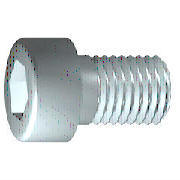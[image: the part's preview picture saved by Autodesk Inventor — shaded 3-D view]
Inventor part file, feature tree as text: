
AUTODESK INVENTOR PART (.ipt)
format: ipt  version: 2022 (Build 260153000, 153)  size: 186,880 bytes
history: native  units: mm (DEFAULTED — no unit token found)
features: sketch x2, other x1, extrude x1, plane x1, fillet x1
ambient origin geometry x7: Origin, YZ Plane, XY Plane, X Axis, Y Axis, Z Axis, Center Point
bodies: Solid1 (feature_tree)
feature tree (6):
  other  "Базовый элемент"
  extrude  "Паз"  Depth=17.0mm
  plane  "Work Plane1"
  fillet  "Fillet2"  Radius=0.276153mm
  sketch  "Эскиз1"
  sketch  "Эскиз2"
